# Revit family: Hager-FW-Hollow_wall-IP30-With_Cover-With_DIN-Hosted-PL-pl
name_source: partatom
category: Electrical Equipment
units: mm (PartAtom-declared; Revit-internal decimal feet)

## family parameters
Cut with Voids When Loaded = No
Host = Face
Maintain Annotation Orientation = Yes
Panel Configuration = Two Columns, Circuits Across
Part Type = Panelboard
Room Calculation Point = No
Round Connector Dimension = Use Diameter
Shared = No

## types (15) — shared parameters
BC_MODEL_ID = 1554251
BC_OBJECT_ID = 513842
BC_OBJECT_VERSION = #5
Code hager = ADD-EC000214_EU
EF000003 - Sposób montażu = Do ścian pustych
EF000007 - Kolor = Biały
EF000024 - Odporność na promieniowanie UV = No
EF000049 - Głębokość = 125 mm  [stored 0.410105 ft]
EF000116 - Numer RAL = 9010
EF000218 - Głębokość wbudowania = 112 mm  [stored 0.367454 ft]
EF001062 - Wykonanie zgodne z Dyrektywą Kompatybilności Elektromagnetycznej EMC = No
EF001088 - Możliwość rozbudowy = Yes
EF001134 - Szyna DIN = Yes
EF004462 - Rodzaj zamknięcia = Inne
EF005474 - Stopień ochrony (IP) = IP30
EF006244 - Transparentna pokrywa/drzwi = No
EF006306 - Z zamkiem = No
EF009212 - Wykonanie/rodzaj pokrywy = Z otworem
EF015776 - Listwa zaciskowa uziemienia = No
EF015941 - Drzwi przepuszczające sygnał = No
ETIM class code = EC000214
ETIM class name = Small distribution board
HG000002-with door or cover-pl = Yes
HG000003-Range-pl = FW
HG000005-Thickness-pl = 2 mm  [stored 0.00656168 ft]
HG000006-Flush mounted-pl = Yes
HG000011-Empty rows from bottom-pl = No
HG000012-Door swing angle-pl = 90.00°
HG000013-Door on the left-pl = No
HG000014-Door on the right-pl = Yes
HG000015-Clearance visibility-pl = Yes
HG000016-Door 3D visibility-pl = Yes
HG000017-Distance between poles-pl = 18 mm  [stored 0.0590551 ft]
HG000060-RAL-number = 9010
HG000099-Onfly Template ID-pl-PL = 507532
Manufacturer = Hager
Name = FW-Hollow_wall-IP30-With_Cover-With_DIN-PL
Name BIM&CO = Electricity
Name hager = ADD_Enclosures_EC000214
Uniformat = Low Tension Service & Dist.
Uniformat code = D501001
zero-valued in all types: Default Elevation, EF001131 - Głębokość wewnętrzna

## per-type parameters (varying)
| type | BC_VARIANT_ID | EF000008 - Szerokość | EF000040 - Wysokość | EF000118 - Z płytą montażową | EF000266 - Liczba rzędów | EF000332 - Wysokość wbudowania | EF000846 - Szerokość wbudowania | EF002950 - Szerokość wyrażona liczbą modułów | EF015777 - Listwa zaciskowa przewodu neutralnego | HG000001-Number of columns-pl | HG000004-Manufacturer reference-pl | HG000007-Number of empty columns-pl | HG000008-Number of empty rows-pl | HG000009-Double swing door-pl | HG000010-Asymmetric doors-pl | HGEF000266-Liczba rzędów | HGEF0002950-Szerokość wyrażona liczbą modułów |
| FW-Hollow_wall_W603_H553_D125_12_Modular_Spacing-FWU32K2 | 1178648 | 603 mm | 553 mm  [stored 1.8143 ft] | Yes | 3 | 502 mm  [stored 1.64698 ft] | 560 mm  [stored 1.83727 ft] | 12 | Yes | 1 | FWU32K2 | 1 | 3 | No | No | 3 | 12 |
| FW-Hollow_wall_W603_H553_D125_26_Modular_Spacing-FWU32M2 | 1178649 | 603 mm | 553 mm  [stored 1.8143 ft] | No | 3 | 502 mm  [stored 1.64698 ft] | 560 mm  [stored 1.83727 ft] | 26 | No | 1 | FWU32M2 | 0 | 0 | No | No | 3 | 26 |
| FW-Hollow_wall_W603_H703_D125_12_Modular_Spacing-FWU42K2 | 1178650 | 603 mm | 703 mm  [stored 2.30643 ft] | Yes | 4 | 652 mm  [stored 2.13911 ft] | 560 mm  [stored 1.83727 ft] | 12 | Yes | 1 | FWU42K2 | 1 | 4 | No | No | 4 | 12 |
| FW-Hollow_wall_W603_H703_D125_26_Modular_Spacing-FWU42M2 | 1178651 | 603 mm | 703 mm  [stored 2.30643 ft] | No | 4 | 652 mm  [stored 2.13911 ft] | 560 mm  [stored 1.83727 ft] | 26 | No | 1 | FWU42M2 | 0 | 0 | No | No | 4 | 26 |
| FW-Hollow_wall_W603_H853_D125_12_Modular_Spacing-FWU52K2 | 1178652 | 603 mm | 853 mm  [stored 2.79856 ft] | Yes | 5 | 802 mm  [stored 2.63123 ft] | 560 mm  [stored 1.83727 ft] | 12 | Yes | 1 | FWU52K2 | 1 | 5 | No | No | 5 | 12 |
| FW-Hollow_wall_W603_H853_D125_26_Modular_Spacing-FWU52M2 | 1178653 | 603 mm | 853 mm  [stored 2.79856 ft] | No | 5 | 802 mm  [stored 2.63123 ft] | 560 mm  [stored 1.83727 ft] | 26 | No | 1 | FWU52M2 | 0 | 0 | No | No | 5 | 26 |
| FW-Hollow_wall_W603_H853_D125_12_Modular_Spacing-FWU52N | 1178654 | 603 mm | 853 mm  [stored 2.79856 ft] | No | 5 | 802 mm  [stored 2.63123 ft] | 560 mm  [stored 1.83727 ft] | 12 | No | 2 | FWU52N | 0 | 2 | No | No | 5 | 12 |
| FW-Hollow_wall_W603_H1003_D125_12_Modular_Spacing-FWU62K2 | 1178655 | 603 mm | 1003 mm  [stored 3.29068 ft] | Yes | 6 | 952 mm  [stored 3.12336 ft] | 560 mm  [stored 1.83727 ft] | 12 | Yes | 1 | FWU62K2 | 1 | 6 | No | No | 6 | 12 |
| FW-Hollow_wall_W603_H1003_D125_26_Modular_Spacing-FWU62M2 | 1178656 | 603 mm | 1003 mm  [stored 3.29068 ft] | No | 6 | 952 mm  [stored 3.12336 ft] | 560 mm  [stored 1.83727 ft] | 26 | No | 1 | FWU62M2 | 0 | 0 | No | No | 6 | 26 |
| FW-Hollow_wall_W603_H1003_D125_12_Modular_Spacing-FWU62N | 1178657 | 603 mm | 1003 mm  [stored 3.29068 ft] | No | 6 | 952 mm  [stored 3.12336 ft] | 560 mm  [stored 1.83727 ft] | 12 | No | 2 | FWU62N | 0 | 2 | No | No | 6 | 12 |
| FW-Hollow_wall_W853_H1003_D125_12_Modular_Spacing-FWU63N | 1178658 | 853 mm  [stored 2.79856 ft] | 1003 mm  [stored 3.29068 ft] | No | 6 | 952 mm  [stored 3.12336 ft] | 810 mm | 12 | No | 3 | FWU63N | 0 | 2 | Yes | Yes | 6 | 12 |
| FW-Hollow_wall_W603_H1153_D125_12_Modular_Spacing-FWU72K2 | 1178659 | 603 mm | 1153 mm | Yes | 7 | 1102 mm  [stored 3.61549 ft] | 560 mm  [stored 1.83727 ft] | 12 | Yes | 1 | FWU72K2 | 1 | 7 | No | No | 7 | 12 |
| FW-Hollow_wall_W603_H1153_D125_26_Modular_Spacing-FWU72M2 | 1178660 | 603 mm | 1153 mm | No | 7 | 1102 mm  [stored 3.61549 ft] | 560 mm  [stored 1.83727 ft] | 26 | No | 1 | FWU72M2 | 0 | 0 | No | No | 7 | 26 |
| FW-Hollow_wall_W603_H1153_D125_12_Modular_Spacing-FWU72N | 1178661 | 603 mm | 1153 mm | No | 7 | 1102 mm  [stored 3.61549 ft] | 560 mm  [stored 1.83727 ft] | 12 | No | 2 | FWU72N | 0 | 2 | No | No | 7 | 12 |
| FW-Hollow_wall_W853_H1153_D125_12_Modular_Spacing-FWU73N | 1178662 | 853 mm  [stored 2.79856 ft] | 1153 mm | No | 7 | 1102 mm  [stored 3.61549 ft] | 810 mm | 12 | No | 3 | FWU73N | 0 | 2 | Yes | Yes | 7 | 12 |

note: column(s) folded — value = type name in every type: Reference

note: [stored X ft] marks values corroborated as IEEE doubles in the binary element streams (Revit-internal decimal feet)

## geometry (parser evidence)
native form markers: Sweep x17
no freeform markers — native parametric forms only
